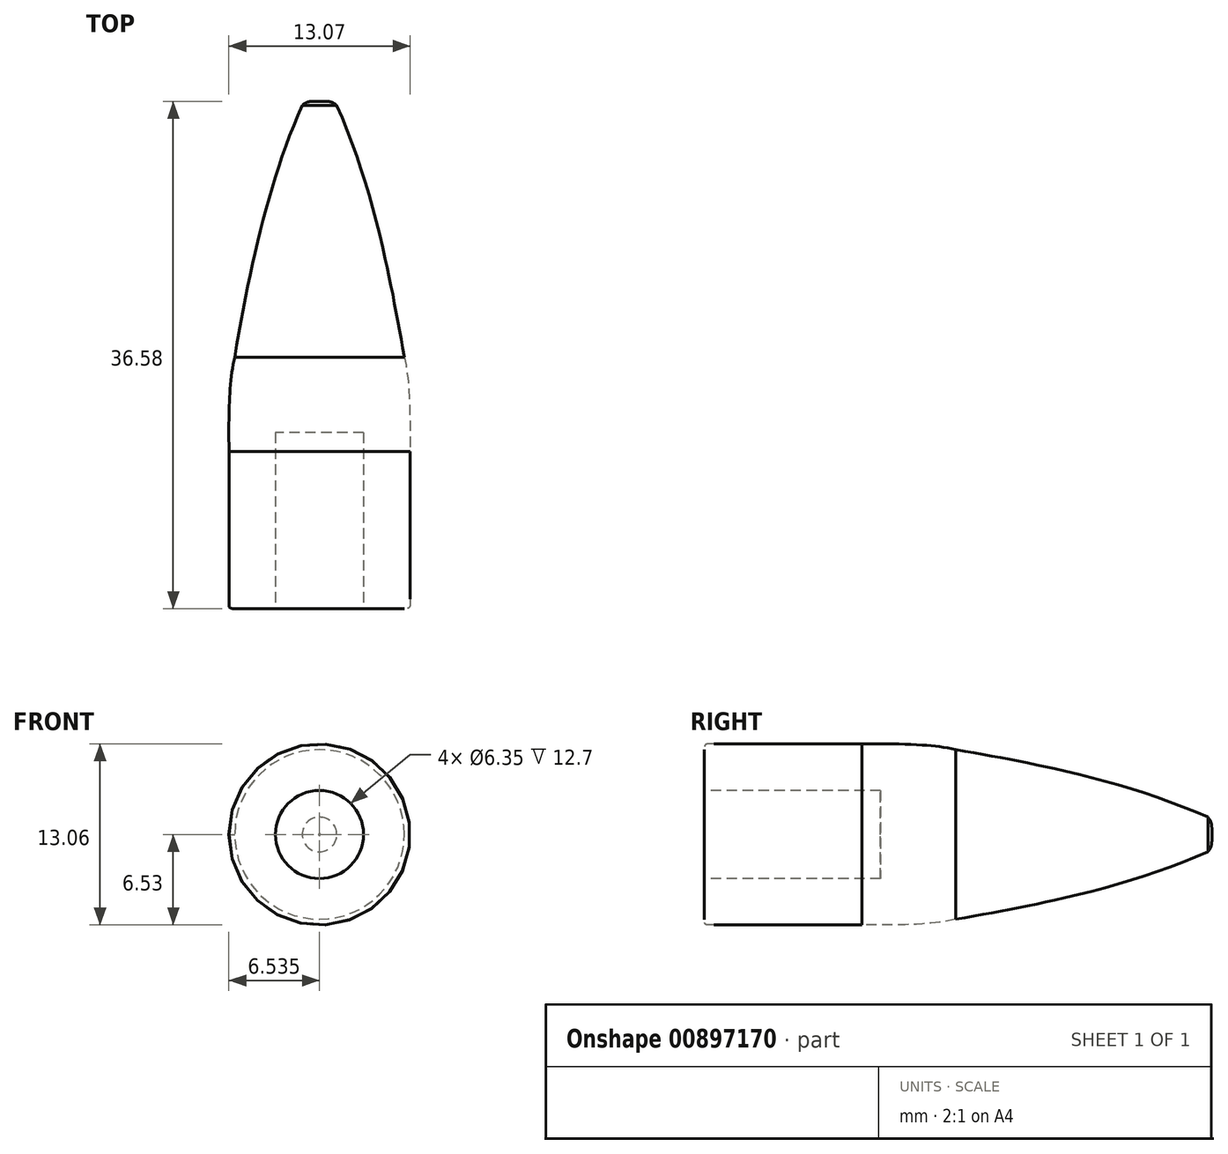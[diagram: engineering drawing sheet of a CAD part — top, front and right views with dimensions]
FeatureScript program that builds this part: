
annotation { "Feature Type Name" : "Feature", "Feature Type Description" : "" }
export const myFeature = defineFeature(function(context is Context, id is Id, definition is map)
    precondition{}
    {
        {
            var Q0;
            Q0=qCreatedBy(makeId("Top.planeOp"),FACE);
            var sketch = newSketch(context, id + "F0", { "sketchPlane" : qUnion([Q0])});
            skLineSegment(sketch, "E0", {"start": v(-15.33, -69.1) * mm, "end": v(-19.13, -69.1) * mm});
            skLineSegment(sketch, "E1", {"start": v(-19.13, -69.1) * mm, "end": v(-19.13, -74.49) * mm});
            skLineSegment(sketch, "E2", {"start": v(-15.33, -74.45) * mm, "end": v(-25.54, -74.45) * mm});
            skLineSegment(sketch, "E3", {"start": v(-25.54, -74.45) * mm, "end": v(-25.54, -72.34) * mm});
            skLineSegment(sketch, "E4", {"start": v(-25.54, -72.34) * mm, "end": v(-23.96, -72.34) * mm});
            skLineSegment(sketch, "E5", {"start": v(-23.96, -72.34) * mm, "end": v(-23.96, -69.58) * mm});
            skLineSegment(sketch, "E6", {"start": v(-23.96, -69.58) * mm, "end": v(-25.54, -68) * mm});
            skLineSegment(sketch, "E7", {"start": v(-25.54, -68) * mm, "end": v(-25.54, 1.9) * mm});
            skLineSegment(sketch, "E8", {"start": v(-22.44, 10.04) * mm, "end": v(-22.44, 26.14) * mm});
            skLineSegment(sketch, "E9", {"start": v(-25.54, -68) * mm, "end": v(-25.54, -70.26) * mm});
            skLineSegment(sketch, "E10", {"start": v(-25.54, 1.9) * mm, "end": v(-22.44, 10.04) * mm});
            skLineSegment(sketch, "E11", {"start": v(-22.44, 26.14) * mm, "end": v(-21.45, 26.14) * mm});
            skLineSegment(sketch, "E12", {"start": v(-15.36, 37.48) * mm, "end": v(-21.85, 37.48) * mm});
            skLineSegment(sketch, "E13", {"start": v(-21.85, 37.48) * mm, "end": v(-21.85, 26.82) * mm});
            skFitSpline(sketch, "E14", {"points": [v(-21.85, 26.82) * mm, v(-21.45, 26.14) * mm], "startDerivative": vector(0, -1.61) * mm, "endDerivative": vector(1.49, 0) * mm});
            skFitSpline(sketch, "E15", {"points": [v(-21.85, 37.48) * mm, v(-21.44, 44.27) * mm], "startDerivative": vector(-0.07, 5.87) * mm, "endDerivative": vector(1.37, 5.74) * mm});
            skLineSegment(sketch, "E16", {"start": v(-15.33, 62.7) * mm, "end": v(-15.33, 26.14) * mm});
            skLineSegment(sketch, "E17", {"start": v(-15.33, -74.45) * mm, "end": v(-15.33, 26.14) * mm});
            skLineSegment(sketch, "E18", {"start": v(-21.45, 26.14) * mm, "end": v(-15.33, 26.14) * mm});
            skLineSegment(sketch, "E19", {"start": v(-15.33, 62.7) * mm, "end": v(-15.39, 62.7) * mm});
            skFitSpline(sketch, "E20", {"points": [v(-15.39, 62.7) * mm, v(-16.57, 62.44) * mm], "startDerivative": vector(-2.53, 0.23) * mm, "endDerivative": vector(-0.47, -0.42) * mm});
            skFitSpline(sketch, "E21", {"points": [v(-16.57, 62.44) * mm, v(-21.44, 44.27) * mm], "startDerivative": vector(-7.34, -16.65) * mm, "endDerivative": vector(-3.47, -20.14) * mm});
            skSolve(sketch);
        }
        {
            var Q0;
            Q0=makeQuery(id+"F0.imprint","IMPRINT",FACE,{"disambiguationData":[TD([[makeQuery(id+"F0.imprint","IMPRINT",EDGE,{"derivedFrom":sQuery(id+"F0.wireOp",EDGE,"E13")}),1.0]])]});
            var Q1;
            Q1=sQuery(id+"F0.wireOp",EDGE,"E16");
            revolve(context, id + "F1", {"surfaceOperationType" : NewSurfaceOperationType.NEW, "entities" : qUnion([Q0]), "axis" : qUnion([Q1]), "revolveType" : RevolveType.FULL});
        }
        {
            var Q0;
            Q0=makeQuery(id+"F1.opRevolve","SWEPT_FACE",FACE,{"disambiguationData":[OSD([sQuery(id+"F0.wireOp",EDGE,"E18")])]});
            var sketch = newSketch(context, id + "F2", { "sketchPlane" : qUnion([Q0])});
            skCircle(sketch, "E22", {"center": v(-15.33, 0) * mm, "radius": 3.18 * mm});
            skSolve(sketch);
        }
        {
            var Q0;
            Q0=makeQuery(id+"F2.imprint","IMPRINT",FACE,{"disambiguationData":[TD([[makeQuery(id+"F2.imprint","IMPRINT",EDGE,{"derivedFrom":sQuery(id+"F2.wireOp",EDGE,"E22")}),1.0]])]});
            extrude(context, id + "F3", {"entities" : qUnion([Q0]), "operationType" : NewBodyOperationType.REMOVE, "oppositeDirection" : true, "depth" : 12.7 * mm, "offsetDistance" : 25.4 * mm});
        }
    });
